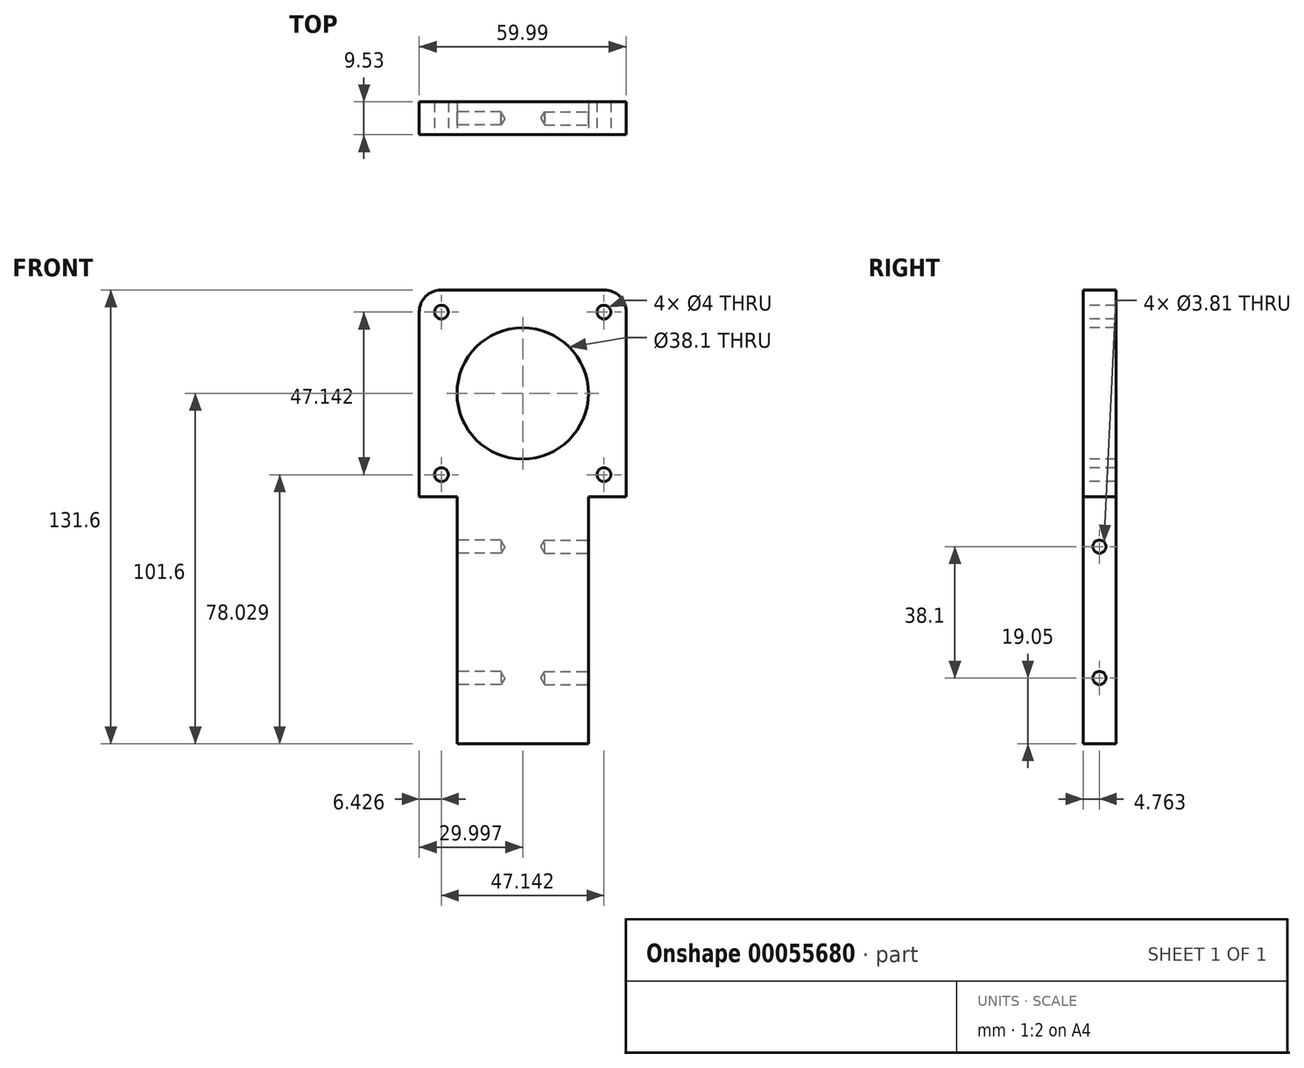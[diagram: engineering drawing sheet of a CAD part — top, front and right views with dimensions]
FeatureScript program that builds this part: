
annotation { "Feature Type Name" : "Feature", "Feature Type Description" : "" }
export const myFeature = defineFeature(function(context is Context, id is Id, definition is map)
    precondition{}
    {
        {
            var Q0;
            Q0=qCreatedBy(makeId("Front.planeOp"),FACE);
            var sketch = newSketch(context, id + "F0", { "sketchPlane" : qUnion([Q0])});
            skLineSegment(sketch, "E0.bottom", {"start": v(0, 0) * mm, "end": v(60, 0) * mm});
            skLineSegment(sketch, "E0.top", {"start": v(0, 131.6) * mm, "end": v(60, 131.6) * mm});
            skLineSegment(sketch, "E0.left", {"start": v(0, 0) * mm, "end": v(0, 131.6) * mm});
            skLineSegment(sketch, "E0.right", {"start": v(60, 0) * mm, "end": v(60, 131.6) * mm});
            skSolve(sketch);
        }
        {
            var Q0;
            Q0 = qSketchRegion(id + "F0", true);
            extrude(context, id + "F1", {"entities" : qUnion([Q0]), "oppositeDirection" : true, "depth" : 9.52 * mm});
        }
        {
            var Q0;
            Q0=makeQuery(id+"F1.opExtrude","CAP_FACE",FACE,{"disambiguationData":[OSD([sQuery(id+"F0.wireOp",EDGE,"E0.bottom"),sQuery(id+"F0.wireOp",EDGE,"E0.top"),sQuery(id+"F0.wireOp",EDGE,"E0.left"),sQuery(id+"F0.wireOp",EDGE,"E0.right")])],"isStart":true});
            var sketch = newSketch(context, id + "F2", { "sketchPlane" : qUnion([Q0])});
            skLineSegment(sketch, "E1", {"start": v(60, 71.6) * mm, "end": v(0, 71.6) * mm});
            skPoint(sketch, "E1.endSnap0", {"position": v(0, 65.8) * mm});
            skLineSegment(sketch, "E2", {"start": v(10.95, 71.6) * mm, "end": v(10.95, 0) * mm});
            skLineSegment(sketch, "E3", {"start": v(49.05, 71.6) * mm, "end": v(49.05, 0) * mm});
            skPoint(sketch, "E4", {"position": v(30, 71.6) * mm});
            skSolve(sketch);
        }
        {
            var Q0;
            Q0=makeQuery(id+"F1.opExtrude","CAP_FACE",FACE,{"disambiguationData":[OSD([sQuery(id+"F0.wireOp",EDGE,"E0.bottom"),sQuery(id+"F0.wireOp",EDGE,"E0.top"),sQuery(id+"F0.wireOp",EDGE,"E0.left"),sQuery(id+"F0.wireOp",EDGE,"E0.right")])],"isStart":true});
            var sketch = newSketch(context, id + "F3", { "sketchPlane" : qUnion([Q0])});
            skLineSegment(sketch, "E5", {"start": v(30, 131.6) * mm, "end": v(30, 0) * mm});
            skPoint(sketch, "E6", {"position": v(30, 101.6) * mm});
            skLineSegment(sketch, "E7", {"start": v(0, 125.17) * mm, "end": v(60, 125.17) * mm});
            skLineSegment(sketch, "E8", {"start": v(0, 78.03) * mm, "end": v(60, 78.03) * mm});
            skLineSegment(sketch, "E9", {"start": v(6.43, 125.17) * mm, "end": v(6.43, 78.03) * mm});
            skLineSegment(sketch, "E10", {"start": v(53.57, 125.17) * mm, "end": v(53.57, 78.03) * mm});
            skCircle(sketch, "E11", {"center": v(30, 101.6) * mm, "radius": 19.05 * mm});
            skSolve(sketch);
        }
        {
            var Q0;
            Q0=sQuery(id+"F3.wireOp",VERTEX,"E9.start");
            var Q1;
            Q1=sQuery(id+"F3.wireOp",VERTEX,"E9.end");
            var Q2;
            Q2=sQuery(id+"F3.wireOp",VERTEX,"E10.end");
            var Q3;
            Q3=sQuery(id+"F3.wireOp",VERTEX,"E10.start");
            var Q4;
            Q4=makeQuery(id+"F1.opExtrude","SWEPT_BODY",BODY,{"disambiguationData":[OSD([sQuery(id+"F0.wireOp",EDGE,"E0.bottom"),sQuery(id+"F0.wireOp",EDGE,"E0.top"),sQuery(id+"F0.wireOp",EDGE,"E0.left"),sQuery(id+"F0.wireOp",EDGE,"E0.right")])]});
            hole(context, id + "F4", {"style" : HoleStyle.SIMPLE, "holeDiameter" : 4 * mm, "endStyle" : HoleEndStyle.THROUGH, "locations" : qUnion([Q0, Q1, Q2, Q3]), "scope" : qUnion([Q4])});
        }
        {
            var Q0;
            {var subQ3=sQuery(id+"F2.wireOp",EDGE,"E2");Q0=makeQuery(id+"F2.imprint","IMPRINT",FACE,{"disambiguationData":[TD([[makeQuery(id+"F2.imprint","IMPRINT",EDGE,{"derivedFrom":subQ3}),-1.0]])]});}
            var Q1;
            {var subQ3=sQuery(id+"F2.wireOp",EDGE,"E3");Q1=makeQuery(id+"F2.imprint","IMPRINT",FACE,{"disambiguationData":[TD([[makeQuery(id+"F2.imprint","IMPRINT",EDGE,{"derivedFrom":subQ3}),1.0]])]});}
            extrude(context, id + "F5", {"entities" : qUnion([Q0, Q1]), "operationType" : NewBodyOperationType.REMOVE, "endBound" : BoundingType.THROUGH_ALL, "oppositeDirection" : true, "depth" : 25.4 * mm});
        }
        {
            var Q0;
            Q0=makeQuery(id+"F1.opExtrude","SWEPT_EDGE",EDGE,{"disambiguationData":[OSD([sQuery(id+"F0.wireOp",EDGE,"E0.top"),sQuery(id+"F0.wireOp",EDGE,"E0.left")])]});
            var Q1;
            Q1=makeQuery(id+"F1.opExtrude","SWEPT_EDGE",EDGE,{"disambiguationData":[OSD([sQuery(id+"F0.wireOp",EDGE,"E0.top"),sQuery(id+"F0.wireOp",EDGE,"E0.right")])]});
            var Q2;
            Q2=makeQuery(id+"F5.boolean.opBoolean","COPY",EDGE,{"derivedFrom":makeQuery(id+"F5.opExtrude","SWEPT_EDGE",EDGE,{"disambiguationData":[OSD([sQuery(id+"F0.wireOp",EDGE,"E0.left"),sQuery(id+"F2.wireOp",EDGE,"E1")])]})});
            var Q3;
            Q3=makeQuery(id+"F5.boolean.opBoolean","COPY",EDGE,{"derivedFrom":makeQuery(id+"F5.opExtrude","SWEPT_EDGE",EDGE,{"disambiguationData":[OSD([sQuery(id+"F0.wireOp",EDGE,"E0.right"),sQuery(id+"F2.wireOp",EDGE,"E1")])]})});
            fillet(context, id + "F6", {"entities" : qUnion([Q0, Q1, Q2, Q3]), "radius" : 6.35 * mm, "tangentPropagation" : true, "allowEdgeOverflow" : false});
        }
        {
            var Q0;
            Q0=makeQuery(id+"F1.opExtrude","CAP_FACE",FACE,{"disambiguationData":[OSD([sQuery(id+"F0.wireOp",EDGE,"E0.bottom"),sQuery(id+"F0.wireOp",EDGE,"E0.top"),sQuery(id+"F0.wireOp",EDGE,"E0.left"),sQuery(id+"F0.wireOp",EDGE,"E0.right")])],"isStart":true});
            var sketch = newSketch(context, id + "F7", { "sketchPlane" : qUnion([Q0])});
            skLineSegment(sketch, "E12", {"start": v(30, 131.6) * mm, "end": v(30, 0) * mm});
            skPoint(sketch, "E13", {"position": v(30, 101.6) * mm});
            skSolve(sketch);
        }
        {
            var Q0;
            Q0=sQuery(id+"F7.wireOp",VERTEX,"E13");
            var Q1;
            Q1=makeQuery(id+"F1.opExtrude","SWEPT_BODY",BODY,{"disambiguationData":[OSD([sQuery(id+"F0.wireOp",EDGE,"E0.bottom"),sQuery(id+"F0.wireOp",EDGE,"E0.top"),sQuery(id+"F0.wireOp",EDGE,"E0.left"),sQuery(id+"F0.wireOp",EDGE,"E0.right")])]});
            hole(context, id + "F8", {"style" : HoleStyle.SIMPLE, "holeDiameter" : 38.1 * mm, "endStyle" : HoleEndStyle.THROUGH, "locations" : qUnion([Q0]), "scope" : qUnion([Q1])});
        }
        {
            var Q0;
            Q0=makeQuery(id+"F5.boolean.opBoolean","COPY",FACE,{"derivedFrom":makeQuery(id+"F5.opExtrude","SWEPT_FACE",FACE,{"disambiguationData":[OSD([sQuery(id+"F2.wireOp",EDGE,"E3")])]})});
            var sketch = newSketch(context, id + "F9", { "sketchPlane" : qUnion([Q0])});
            skLineSegment(sketch, "E14", {"start": v(4.76, 0) * mm, "end": v(4.76, 71.6) * mm});
            skPoint(sketch, "E15", {"position": v(4.76, 71.6) * mm});
            skPoint(sketch, "E16", {"position": v(4.76, 57.15) * mm});
            skPoint(sketch, "E17", {"position": v(4.76, 19.05) * mm});
            skSolve(sketch);
        }
        {
            var Q0;
            Q0=sQuery(id+"F9.wireOp",VERTEX,"E16");
            var Q1;
            Q1=sQuery(id+"F9.wireOp",VERTEX,"E17");
            var Q2;
            Q2=makeQuery(id+"F1.opExtrude","SWEPT_BODY",BODY,{"disambiguationData":[OSD([sQuery(id+"F0.wireOp",EDGE,"E0.bottom"),sQuery(id+"F0.wireOp",EDGE,"E0.top"),sQuery(id+"F0.wireOp",EDGE,"E0.left"),sQuery(id+"F0.wireOp",EDGE,"E0.right")])]});
            hole(context, id + "F10", {"style" : HoleStyle.SIMPLE, "holeDiameter" : 3.8 * mm, "endStyle" : HoleEndStyle.BLIND, "holeDepth" : 12.7 * mm, "locations" : qUnion([Q0, Q1]), "scope" : qUnion([Q2])});
        }
        {
            var Q0;
            Q0=makeQuery(id+"F5.boolean.opBoolean","COPY",FACE,{"derivedFrom":makeQuery(id+"F5.opExtrude","SWEPT_FACE",FACE,{"disambiguationData":[OSD([sQuery(id+"F2.wireOp",EDGE,"E2")])]})});
            var sketch = newSketch(context, id + "F11", { "sketchPlane" : qUnion([Q0])});
            skLineSegment(sketch, "E18", {"start": v(-4.76, 71.6) * mm, "end": v(-4.76, 0) * mm});
            skPoint(sketch, "E19", {"position": v(-4.76, 57.15) * mm});
            skPoint(sketch, "E20", {"position": v(-4.76, 19.05) * mm});
            skSolve(sketch);
        }
        {
            var Q0;
            Q0=sQuery(id+"F11.wireOp",VERTEX,"E19");
            var Q1;
            Q1=sQuery(id+"F11.wireOp",VERTEX,"E20");
            var Q2;
            Q2=makeQuery(id+"F1.opExtrude","SWEPT_BODY",BODY,{"disambiguationData":[OSD([sQuery(id+"F0.wireOp",EDGE,"E0.bottom"),sQuery(id+"F0.wireOp",EDGE,"E0.top"),sQuery(id+"F0.wireOp",EDGE,"E0.left"),sQuery(id+"F0.wireOp",EDGE,"E0.right")])]});
            hole(context, id + "F12", {"style" : HoleStyle.SIMPLE, "holeDiameter" : 3.8 * mm, "endStyle" : HoleEndStyle.BLIND, "holeDepth" : 12.7 * mm, "locations" : qUnion([Q0, Q1]), "scope" : qUnion([Q2])});
        }
    });
